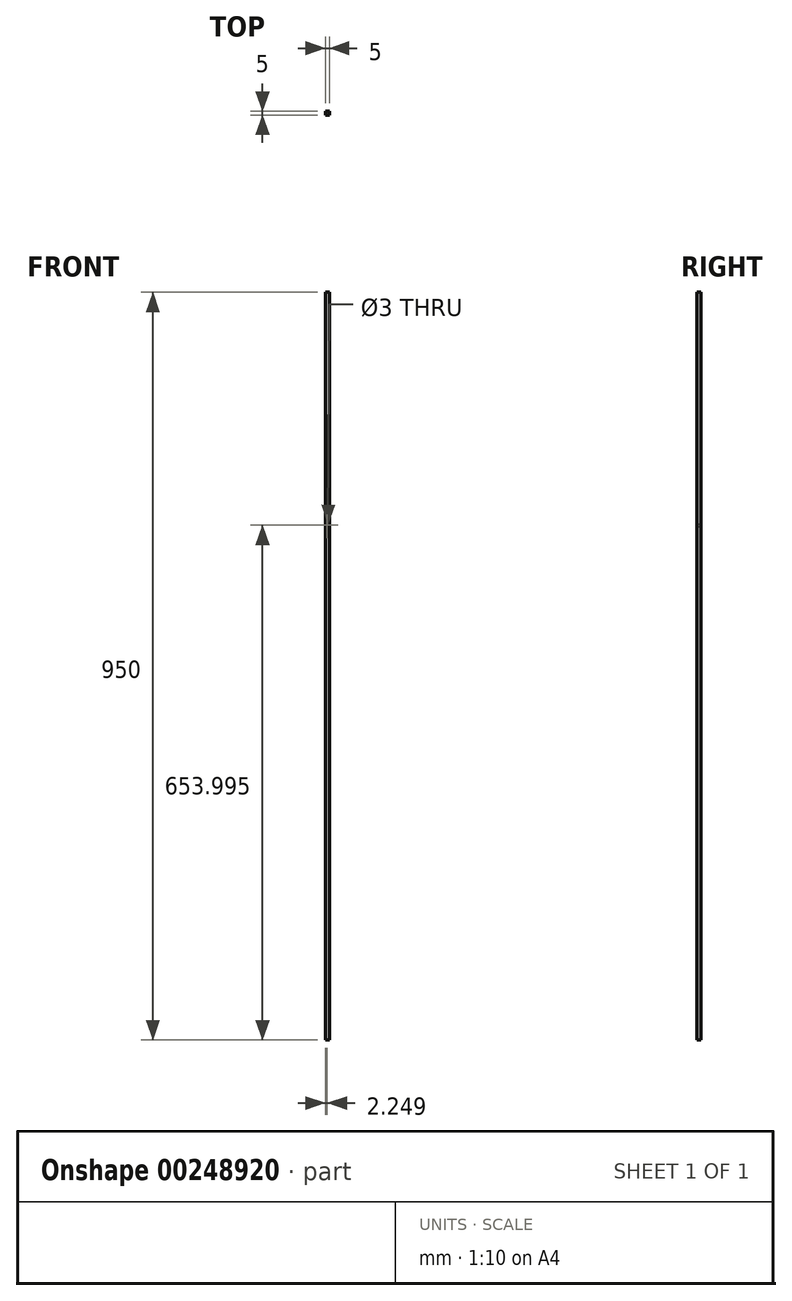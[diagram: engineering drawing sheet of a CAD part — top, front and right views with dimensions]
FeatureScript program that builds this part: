
annotation { "Feature Type Name" : "Feature", "Feature Type Description" : "" }
export const myFeature = defineFeature(function(context is Context, id is Id, definition is map)
    precondition{}
    {
        {
            var Q0;
            Q0=qCreatedBy(makeId("Front.planeOp"),FACE);
            var sketch = newSketch(context, id + "F0", { "sketchPlane" : qUnion([Q0])});
            skLineSegment(sketch, "E0", {"start": v(62.34, 12.72) * mm, "end": v(-131.55, 12.72) * mm, "construction": true});
            skLineSegment(sketch, "E1.bottom", {"start": v(-61.8, 983.67) * mm, "end": v(-56.8, 983.67) * mm});
            skLineSegment(sketch, "E1.top", {"start": v(-61.8, 33.67) * mm, "end": v(-56.8, 33.67) * mm});
            skLineSegment(sketch, "E1.left", {"start": v(-61.8, 983.67) * mm, "end": v(-61.8, 33.67) * mm});
            skLineSegment(sketch, "E1.right", {"start": v(-56.8, 983.67) * mm, "end": v(-56.8, 33.67) * mm});
            skCircle(sketch, "E2", {"center": v(-59.54, 687.67) * mm, "radius": 1.5 * mm});
            skSolve(sketch);
        }
        {
            var Q0;
            Q0=makeQuery(id+"F0.imprint","IMPRINT",FACE,{"disambiguationData":[TD([[makeQuery(id+"F0.imprint","IMPRINT",EDGE,{"derivedFrom":sQuery(id+"F0.wireOp",EDGE,"E1.bottom")}),-1.0]])]});
            extrude(context, id + "F1", {"entities" : qUnion([Q0]), "depth" : 5 * mm});
        }
    });
